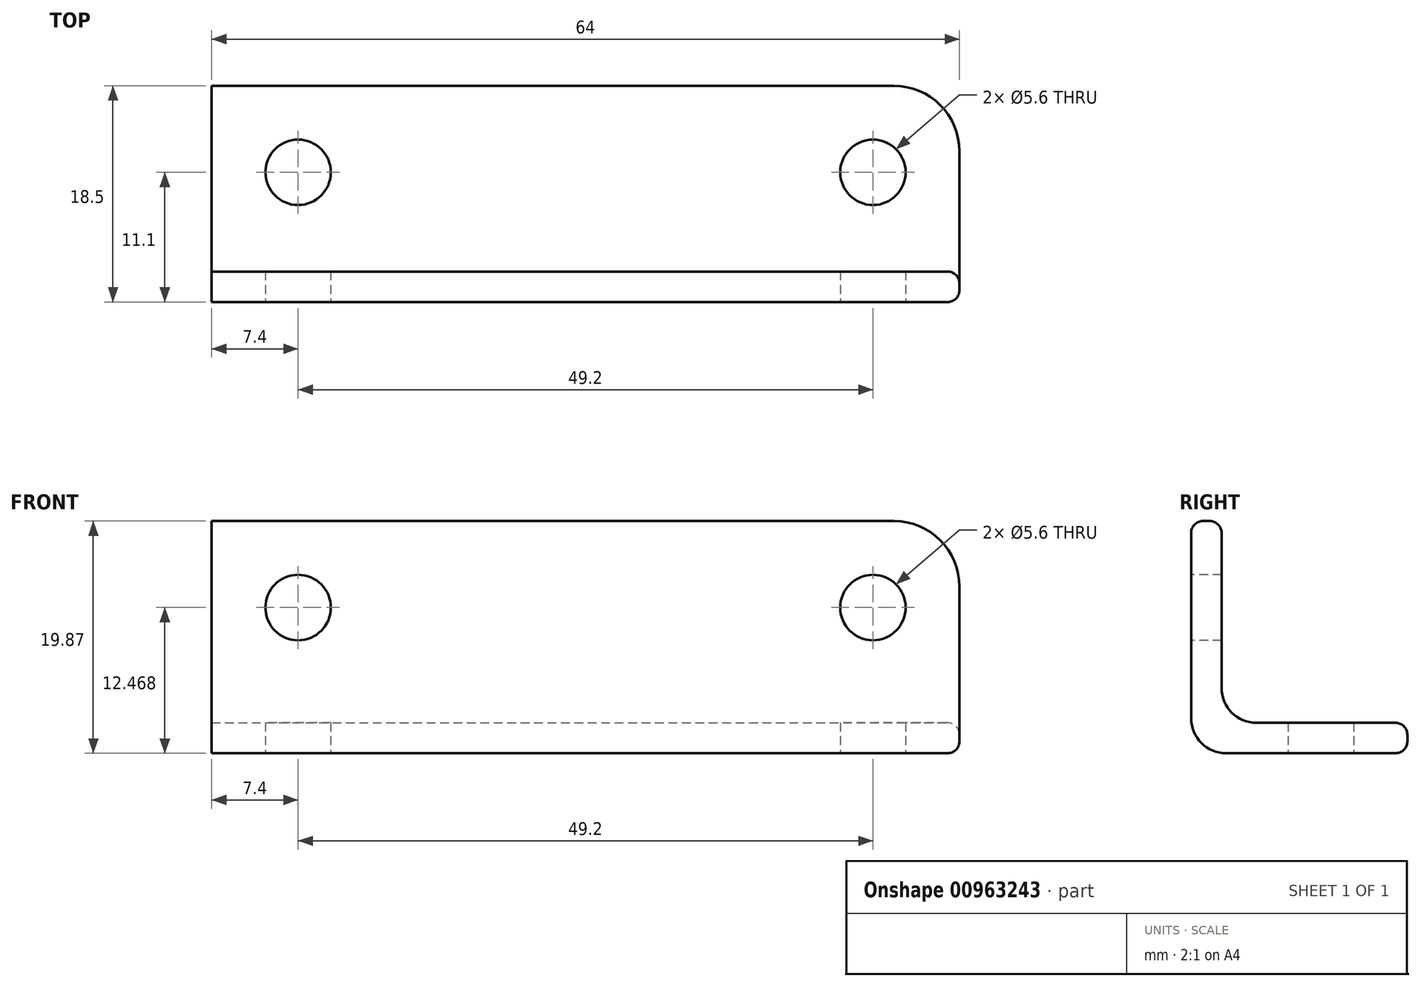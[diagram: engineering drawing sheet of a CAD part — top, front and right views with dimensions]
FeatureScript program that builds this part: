
annotation { "Feature Type Name" : "Feature", "Feature Type Description" : "" }
export const myFeature = defineFeature(function(context is Context, id is Id, definition is map)
    precondition{}
    {
        {
            var Q0;
            Q0=qCreatedBy(makeId("Top.planeOp"),FACE);
            var sketch = newSketch(context, id + "F0", { "sketchPlane" : qUnion([Q0])});
            skLineSegment(sketch, "E0.bottom", {"start": v(0, 0) * mm, "end": v(64, 0) * mm});
            skLineSegment(sketch, "E0.top", {"start": v(0, 18.5) * mm, "end": v(58.4, 18.5) * mm});
            skLineSegment(sketch, "E0.left", {"start": v(0, 0) * mm, "end": v(0, 18.5) * mm});
            skLineSegment(sketch, "E0.right", {"start": v(64, 0) * mm, "end": v(64, 12.9) * mm});
            skCircle(sketch, "E1", {"center": v(7.4, 11.1) * mm, "radius": 2.8 * mm});
            skCircle(sketch, "E2", {"center": v(56.6, 11.1) * mm, "radius": 2.8 * mm});
            skPoint(sketch, "E3.visualSharp", {"position": v(0, 18.5) * mm});
            skPoint(sketch, "E4.visualSharp", {"position": v(64, 18.5) * mm});
            skArc(sketch, "E4.filletArc", {"start": v(64, 12.9) * mm, "mid": v(62.36, 16.86) * mm, "end": v(58.4, 18.5) * mm});
            skSolve(sketch);
        }
        {
            var Q0;
            Q0=makeQuery(id+"F0.imprint","IMPRINT",FACE,{"disambiguationData":[TD([[makeQuery(id+"F0.imprint","IMPRINT",EDGE,{"derivedFrom":sQuery(id+"F0.wireOp",EDGE,"E0.bottom")}),1.0]])]});
            extrude(context, id + "F1", {"entities" : qUnion([Q0]), "depth" : 2.6 * mm, "offsetDistance" : 25 * mm});
        }
        {
            var Q0;
            Q0=qCreatedBy(makeId("Front.planeOp"),FACE);
            var sketch = newSketch(context, id + "F2", { "sketchPlane" : qUnion([Q0])});
            skLineSegment(sketch, "E5.bottom", {"start": v(0, 1.37) * mm, "end": v(64, 1.37) * mm});
            skLineSegment(sketch, "E5.top", {"start": v(0, 19.87) * mm, "end": v(58.4, 19.87) * mm});
            skLineSegment(sketch, "E5.left", {"start": v(0, 1.37) * mm, "end": v(0, 19.87) * mm});
            skLineSegment(sketch, "E5.right", {"start": v(64, 1.37) * mm, "end": v(64, 14.27) * mm});
            skCircle(sketch, "E6", {"center": v(7.4, 12.47) * mm, "radius": 2.8 * mm});
            skCircle(sketch, "E7", {"center": v(56.6, 12.47) * mm, "radius": 2.8 * mm});
            skPoint(sketch, "E8.visualSharp", {"position": v(0, 19.87) * mm});
            skPoint(sketch, "E9.visualSharp", {"position": v(64, 19.87) * mm});
            skArc(sketch, "E9.filletArc", {"start": v(64, 14.27) * mm, "mid": v(62.36, 18.23) * mm, "end": v(58.4, 19.87) * mm});
            skSolve(sketch);
        }
        {
            var Q0;
            Q0 = qSketchRegion(id + "F2", true);
            extrude(context, id + "F3", {"entities" : qUnion([Q0]), "operationType" : NewBodyOperationType.ADD, "oppositeDirection" : true, "depth" : 2.6 * mm, "offsetDistance" : 25 * mm});
        }
        {
            var Q0;
            Q0=makeQuery(id+"F1.opExtrude","CAP_EDGE",EDGE,{"disambiguationData":[OSD([sQuery(id+"F0.wireOp",EDGE,"E0.bottom")])],"isStart":true});
            var Q1;
            Q1=makeQuery(id+"F3.boolean.opBoolean","INTERSECT",EDGE,{"derivedFrom":[makeQuery(id+"F1.opExtrude","CAP_FACE",FACE,{"disambiguationData":[OSD([sQuery(id+"F0.wireOp",EDGE,"E0.bottom"),sQuery(id+"F0.wireOp",EDGE,"E0.top"),sQuery(id+"F0.wireOp",EDGE,"E0.left"),sQuery(id+"F0.wireOp",EDGE,"E0.right"),sQuery(id+"F0.wireOp",EDGE,"E1"),sQuery(id+"F0.wireOp",EDGE,"E2"),sQuery(id+"F0.wireOp",EDGE,"E3.filletArc"),sQuery(id+"F0.wireOp",EDGE,"E4.filletArc")])],"isStart":false}),makeQuery(id+"F3.opExtrude","CAP_FACE",FACE,{"disambiguationData":[OSD([sQuery(id+"F2.wireOp",EDGE,"E5.bottom"),sQuery(id+"F2.wireOp",EDGE,"E5.top"),sQuery(id+"F2.wireOp",EDGE,"E5.left"),sQuery(id+"F2.wireOp",EDGE,"E5.right"),sQuery(id+"F2.wireOp",EDGE,"E6"),sQuery(id+"F2.wireOp",EDGE,"E7"),sQuery(id+"F2.wireOp",EDGE,"E8.filletArc"),sQuery(id+"F2.wireOp",EDGE,"E9.filletArc")])],"isStart":false})]});
            fillet(context, id + "F4", {"entities" : qUnion([Q0, Q1]), "radius" : 3 * mm, "tangentPropagation" : true, "allowEdgeOverflow" : false});
        }
        {
            var Q0;
            Q0=makeQuery(id+"F3.opExtrude","CAP_EDGE",EDGE,{"disambiguationData":[OSD([sQuery(id+"F2.wireOp",EDGE,"E5.top")])],"isStart":false});
            var Q1;
            Q1=makeQuery(id+"F3.opExtrude","CAP_EDGE",EDGE,{"disambiguationData":[OSD([sQuery(id+"F2.wireOp",EDGE,"E5.top")])],"isStart":true});
            var Q2;
            Q2=makeQuery(id+"F1.opExtrude","CAP_EDGE",EDGE,{"disambiguationData":[OSD([sQuery(id+"F0.wireOp",EDGE,"E0.top")])],"isStart":false});
            var Q3;
            Q3=makeQuery(id+"F1.opExtrude","CAP_EDGE",EDGE,{"disambiguationData":[OSD([sQuery(id+"F0.wireOp",EDGE,"E0.top")])],"isStart":true});
            var Q4;
            Q4=makeQuery(id+"F3.boolean.opBoolean","MERGE",EDGE,{"derivedFrom":[makeQuery(id+"F1.opExtrude","SWEPT_EDGE",EDGE,{"disambiguationData":[OSD([sQuery(id+"F0.wireOp",EDGE,"E0.bottom"),sQuery(id+"F0.wireOp",EDGE,"E0.right")])]}),makeQuery(id+"F3.opExtrude","CAP_EDGE",EDGE,{"disambiguationData":[OSD([sQuery(id+"F2.wireOp",EDGE,"E5.right")])],"isStart":true})]});
            var Q5;
            Q5=makeQuery(id+"F4.opFillet","BLEND_EDGE",EDGE,{"blendedFrom":[makeQuery(id+"F1.opExtrude","CAP_EDGE",EDGE,{"disambiguationData":[OSD([sQuery(id+"F0.wireOp",EDGE,"E0.bottom")])],"isStart":true}),makeQuery(id+"F3.boolean.opBoolean","MERGE",FACE,{"derivedFrom":[makeQuery(id+"F1.opExtrude","SWEPT_FACE",FACE,{"disambiguationData":[OSD([sQuery(id+"F0.wireOp",EDGE,"E0.right")])]}),makeQuery(id+"F3.opExtrude","SWEPT_FACE",FACE,{"disambiguationData":[OSD([sQuery(id+"F2.wireOp",EDGE,"E5.right")])]})]})],"blendedInto":[makeQuery(id+"F3.boolean.opBoolean","MERGE",FACE,{"derivedFrom":[makeQuery(id+"F1.opExtrude","SWEPT_FACE",FACE,{"disambiguationData":[OSD([sQuery(id+"F0.wireOp",EDGE,"E0.right")])]}),makeQuery(id+"F3.opExtrude","SWEPT_FACE",FACE,{"disambiguationData":[OSD([sQuery(id+"F2.wireOp",EDGE,"E5.right")])]})]})]});
            var Q6;
            Q6=makeQuery(id+"F1.opExtrude","CAP_EDGE",EDGE,{"disambiguationData":[OSD([sQuery(id+"F0.wireOp",EDGE,"E0.right")])],"isStart":true});
            var Q7;
            Q7=makeQuery(id+"F1.opExtrude","CAP_EDGE",EDGE,{"disambiguationData":[OSD([sQuery(id+"F0.wireOp",EDGE,"E0.right")])],"isStart":false});
            var Q8;
            Q8=makeQuery(id+"F3.opExtrude","CAP_EDGE",EDGE,{"disambiguationData":[OSD([sQuery(id+"F2.wireOp",EDGE,"E5.right")])],"isStart":false});
            var Q9;
            Q9=makeQuery(id+"F3.opExtrude","CAP_EDGE",EDGE,{"disambiguationData":[OSD([sQuery(id+"F2.wireOp",EDGE,"E9.filletArc")])],"isStart":false});
            var Q10;
            Q10=makeQuery(id+"F3.opExtrude","CAP_EDGE",EDGE,{"disambiguationData":[OSD([sQuery(id+"F2.wireOp",EDGE,"E9.filletArc")])],"isStart":true});
            var Q11;
            Q11=makeQuery(id+"F1.opExtrude","CAP_EDGE",EDGE,{"disambiguationData":[OSD([sQuery(id+"F0.wireOp",EDGE,"E4.filletArc")])],"isStart":false});
            var Q12;
            Q12=makeQuery(id+"F1.opExtrude","CAP_EDGE",EDGE,{"disambiguationData":[OSD([sQuery(id+"F0.wireOp",EDGE,"E4.filletArc")])],"isStart":true});
            fillet(context, id + "F5", {"entities" : qUnion([Q0, Q1, Q2, Q3, Q4, Q5, Q6, Q7, Q8, Q9, Q10, Q11, Q12]), "radius" : 1 * mm, "allowEdgeOverflow" : false});
        }
    });
